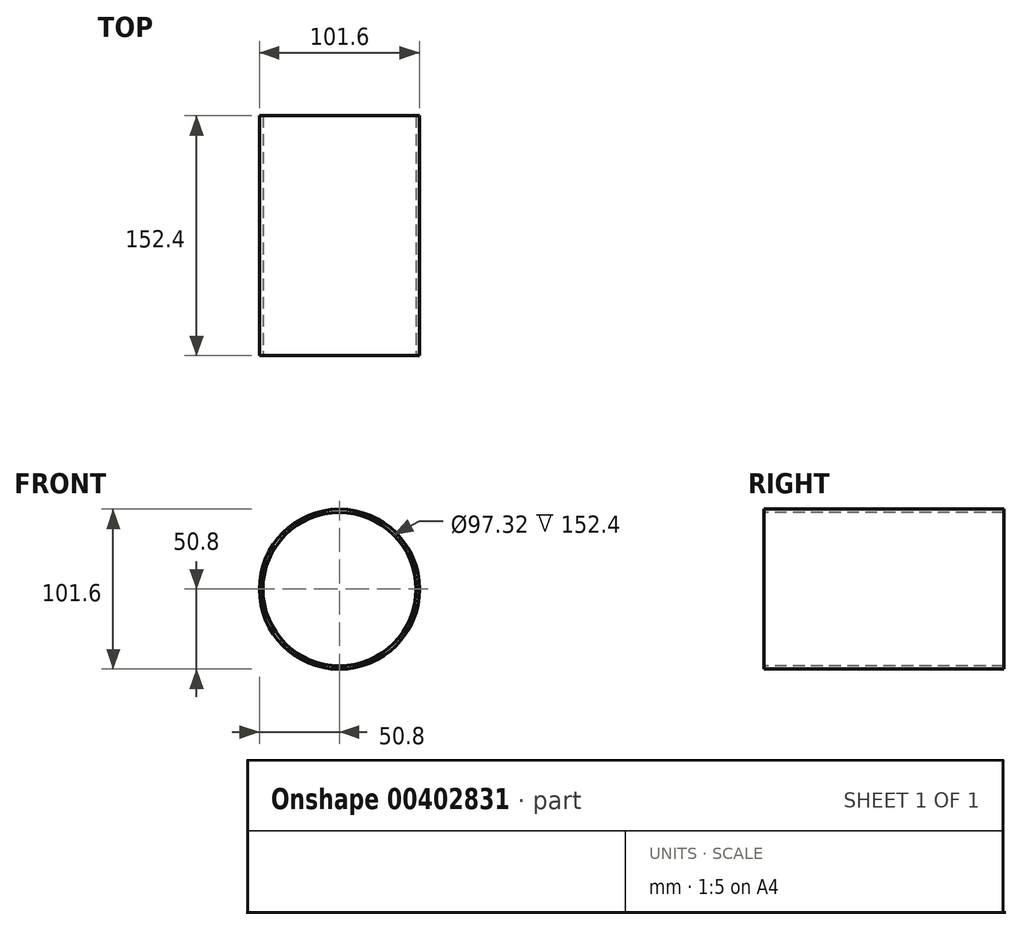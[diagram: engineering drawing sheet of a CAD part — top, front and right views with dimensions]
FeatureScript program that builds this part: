
annotation { "Feature Type Name" : "Feature", "Feature Type Description" : "" }
export const myFeature = defineFeature(function(context is Context, id is Id, definition is map)
    precondition{}
    {
        {
            var Q0;
            Q0=qCreatedBy(makeId("Front.planeOp"),FACE);
            var sketch = newSketch(context, id + "F0", { "sketchPlane" : qUnion([Q0])});
            skCircle(sketch, "E0", {"center": v(0, 0) * mm, "radius": 50.8 * mm});
            skSolve(sketch);
        }
        {
            var Q0;
            Q0 = qSketchRegion(id + "F0", true);
            extrude(context, id + "F1", {"entities" : qUnion([Q0]), "depth" : 152.4 * mm});
        }
        {
            var Q0;
            Q0=makeQuery(id+"F1.opExtrude","CAP_FACE",FACE,{"disambiguationData":[OSD([sQuery(id+"F0.wireOp",EDGE,"E0")])],"isStart":false});
            var sketch = newSketch(context, id + "F2", { "sketchPlane" : qUnion([Q0])});
            skCircle(sketch, "E1", {"center": v(0, 0) * mm, "radius": 48.66 * mm});
            skSolve(sketch);
        }
        {
            var Q0;
            Q0=makeQuery(id+"F2.imprint","IMPRINT",FACE,{"disambiguationData":[TD([[makeQuery(id+"F2.imprint","IMPRINT",EDGE,{"derivedFrom":sQuery(id+"F2.wireOp",EDGE,"E1")}),1.0]])]});
            extrude(context, id + "F3", {"entities" : qUnion([Q0]), "operationType" : NewBodyOperationType.REMOVE, "oppositeDirection" : true, "depth" : 139.7 * mm});
        }
        {
            var Q0;
            Q0=makeQuery(id+"F2.imprint","IMPRINT",FACE,{"disambiguationData":[TD([[makeQuery(id+"F2.imprint","IMPRINT",EDGE,{"derivedFrom":sQuery(id+"F2.wireOp",EDGE,"E1")}),1.0]])]});
            var Q1;
            Q1=makeQuery(id+"F3.boolean.opBoolean","COPY",FACE,{"derivedFrom":makeQuery(id+"F3.opExtrude","CAP_FACE",FACE,{"disambiguationData":[OSD([sQuery(id+"F2.wireOp",EDGE,"E1")])],"isStart":false})});
            extrude(context, id + "F4", {"entities" : qUnion([Q0, Q1]), "operationType" : NewBodyOperationType.REMOVE, "oppositeDirection" : true, "depth" : 139.7 * mm});
        }
    });
